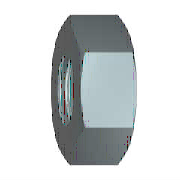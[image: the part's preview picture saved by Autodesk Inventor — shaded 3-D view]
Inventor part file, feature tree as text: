
AUTODESK INVENTOR PART (.ipt)
format: ipt  version: 2018 (Build 220112000, 112)  size: 172,032 bytes
history: native  units: mm (DEFAULTED — no unit token found)
features: sketch x3, other x2, extrude x1, hole x1, plane x1
ambient origin geometry x7: Origin, YZ Plane, XZ Plane, X Axis, Y Axis, Z Axis, Center Point
bodies: Solid1 (feature_tree)
feature tree (8):
  extrude  "Corpo"  Depth=15.011107mm
  other  "Smusso1"
  hole  "Filettatura"  [1 undecoded]
  other  "Work Axis1"
  plane  "Work Plane1"
  sketch  "Schizzo1"
  sketch  "Schizzo2"
  sketch  "Schizzo3"
note: 1 required parameter value undecoded (feature->parameter linkage not recoverable at this tier; creation-order binding heuristic only, values carry confidence <= 0.55)
